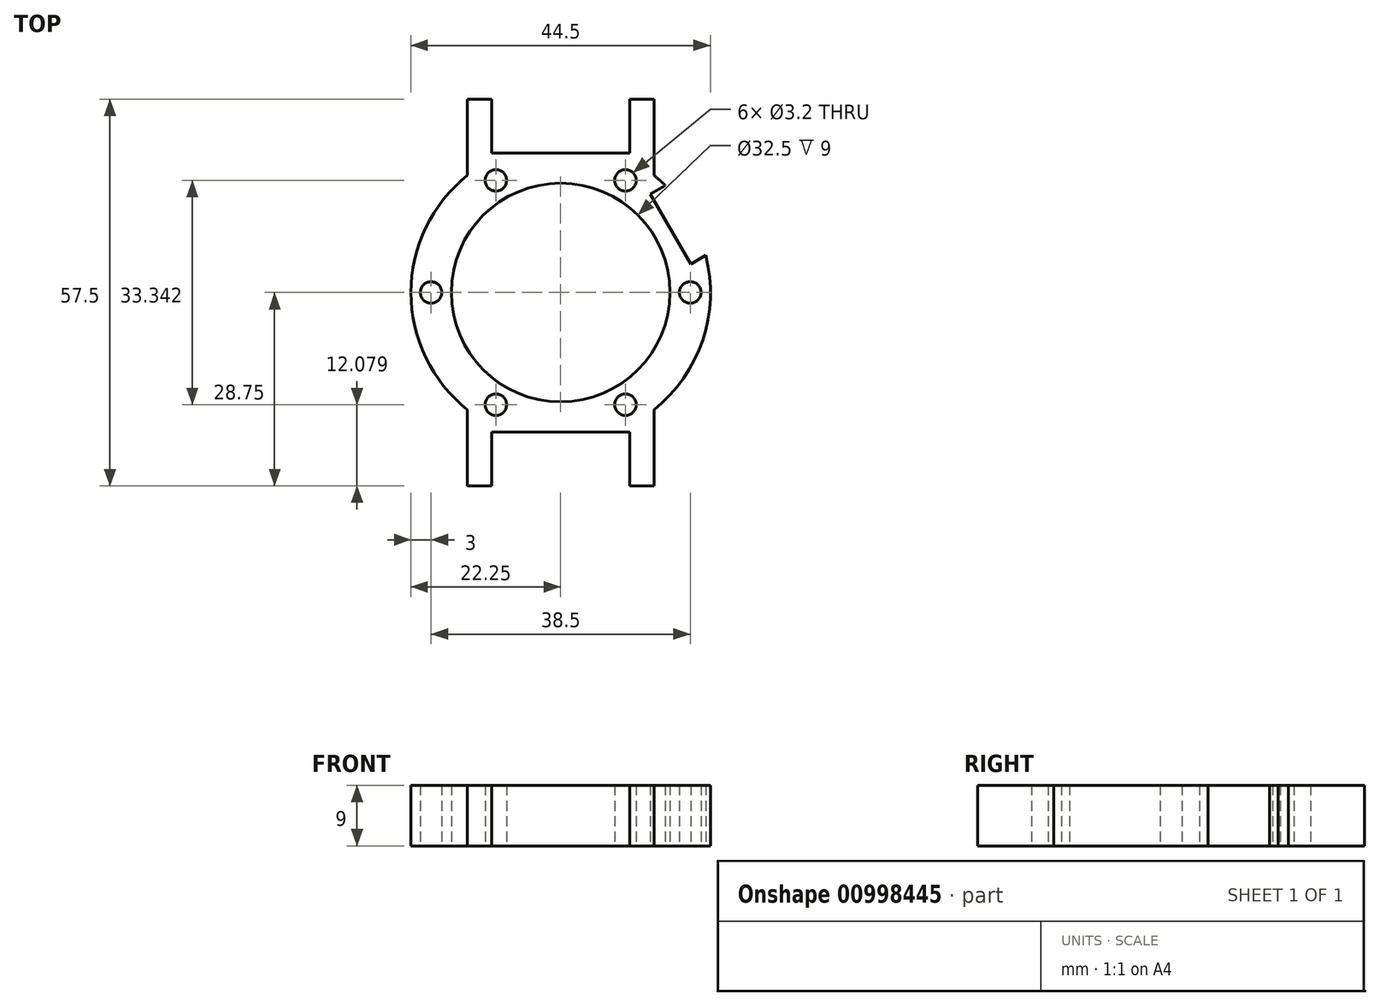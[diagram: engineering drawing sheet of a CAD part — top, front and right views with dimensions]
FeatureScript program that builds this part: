
annotation { "Feature Type Name" : "Feature", "Feature Type Description" : "" }
export const myFeature = defineFeature(function(context is Context, id is Id, definition is map)
    precondition{}
    {
        {
            var Q0;
            Q0=qCreatedBy(makeId("Top.planeOp"),FACE);
            var sketch = newSketch(context, id + "F0", { "sketchPlane" : qUnion([Q0])});
            skCircle(sketch, "E0.cCircle", {"center": v(0, 0) * mm, "radius": 16.67 * mm, "construction": true});
            skLineSegment(sketch, "E0.0", {"start": v(9.62, -16.67) * mm, "end": v(-9.62, -16.67) * mm, "construction": true});
            skLineSegment(sketch, "E0.1", {"start": v(-9.62, -16.67) * mm, "end": v(-19.25, 0) * mm, "construction": true});
            skLineSegment(sketch, "E0.2", {"start": v(-19.25, 0) * mm, "end": v(-9.62, 16.67) * mm, "construction": true});
            skLineSegment(sketch, "E0.3", {"start": v(-9.63, 16.67) * mm, "end": v(9.62, 16.67) * mm, "construction": true});
            skLineSegment(sketch, "E0.4", {"start": v(9.62, 16.67) * mm, "end": v(19.25, 0) * mm, "construction": true});
            skLineSegment(sketch, "E0.5", {"start": v(19.25, 0) * mm, "end": v(9.62, -16.67) * mm, "construction": true});
            skPoint(sketch, "E0.0.midPoint", {"position": v(0, -16.67) * mm});
            skCircle(sketch, "E1", {"center": v(0, 0) * mm, "radius": 16.25 * mm});
            skCircle(sketch, "E2", {"center": v(0, 0) * mm, "radius": 22.25 * mm});
            skLineSegment(sketch, "E3.bottom", {"start": v(10.25, 20.75) * mm, "end": v(-10.25, 20.75) * mm});
            skLineSegment(sketch, "E3.top", {"start": v(10.25, 28.75) * mm, "end": v(-10.25, 28.75) * mm});
            skLineSegment(sketch, "E3.left", {"start": v(10.25, 20.75) * mm, "end": v(10.25, 28.75) * mm});
            skLineSegment(sketch, "E3.right", {"start": v(-10.25, 20.75) * mm, "end": v(-10.25, 28.75) * mm});
            skPoint(sketch, "E3.middle", {"position": v(0, 24.75) * mm});
            skLineSegment(sketch, "E4.bottom", {"start": v(13.85, 28.75) * mm, "end": v(-13.85, 28.75) * mm});
            skLineSegment(sketch, "E4.top", {"start": v(13.85, 17.41) * mm, "end": v(-13.85, 17.41) * mm});
            skLineSegment(sketch, "E4.left", {"start": v(13.85, 28.75) * mm, "end": v(13.85, 17.41) * mm});
            skLineSegment(sketch, "E4.right", {"start": v(-13.85, 28.75) * mm, "end": v(-13.85, 17.41) * mm});
            skPoint(sketch, "E4.middle", {"position": v(0, 23.08) * mm});
            skLineSegment(sketch, "E5.bottom", {"start": v(10.25, -28.75) * mm, "end": v(-10.25, -28.75) * mm});
            skLineSegment(sketch, "E5.top", {"start": v(10.25, -20.75) * mm, "end": v(-10.25, -20.75) * mm});
            skLineSegment(sketch, "E5.left", {"start": v(10.25, -28.75) * mm, "end": v(10.25, -20.75) * mm});
            skLineSegment(sketch, "E5.right", {"start": v(-10.25, -28.75) * mm, "end": v(-10.25, -20.75) * mm});
            skPoint(sketch, "E5.middle", {"position": v(0, -24.75) * mm});
            skLineSegment(sketch, "E6.bottom", {"start": v(13.85, -28.75) * mm, "end": v(-13.85, -28.75) * mm});
            skLineSegment(sketch, "E6.top", {"start": v(13.85, -17.41) * mm, "end": v(-13.85, -17.41) * mm});
            skLineSegment(sketch, "E6.left", {"start": v(13.85, -28.75) * mm, "end": v(13.85, -17.41) * mm});
            skLineSegment(sketch, "E6.right", {"start": v(-13.85, -28.75) * mm, "end": v(-13.85, -17.41) * mm});
            skPoint(sketch, "E6.middle", {"position": v(0, -23.08) * mm});
            skLineSegment(sketch, "E7", {"start": v(13.32, 14.62) * mm, "end": v(19.32, 4.23) * mm});
            skLineSegment(sketch, "E8", {"start": v(13.32, 14.62) * mm, "end": v(15.56, 15.9) * mm});
            skLineSegment(sketch, "E9", {"start": v(19.32, 4.23) * mm, "end": v(21.56, 5.52) * mm});
            skLineSegment(sketch, "E10", {"start": v(13.32, 14.62) * mm, "end": v(0, 0) * mm, "construction": true});
            skLineSegment(sketch, "E11", {"start": v(0, 0) * mm, "end": v(19.32, 4.23) * mm, "construction": true});
            skSolve(sketch);
        }
        {
            var Q0;
            Q0=makeQuery(id+"F0.imprint","IMPRINT",FACE,{"disambiguationData":[TD([[makeQuery(id+"F0.imprint","IMPRINT",EDGE,{"derivedFrom":sQuery(id+"F0.wireOp",EDGE,"E1")}),-1.0]])]});
            var Q1;
            {var subQ1=sQuery(id+"F0.wireOp",EDGE,"E5.right");Q1=makeQuery(id+"F0.imprint","IMPRINT",FACE,{"disambiguationData":[TD([[makeQuery(id+"F0.imprint","IMPRINT",EDGE,{"derivedFrom":subQ1}),1.0]])]});}
            var Q2;
            {var subQ0=sQuery(id+"F0.wireOp",EDGE,"E6.top");Q2=makeQuery(id+"F0.imprint","IMPRINT",FACE,{"disambiguationData":[TD([[makeQuery(id+"F0.imprint","IMPRINT",EDGE,{"derivedFrom":subQ0}),1.0]])]});}
            var Q3;
            {var subQ1=sQuery(id+"F0.wireOp",EDGE,"E5.left");Q3=makeQuery(id+"F0.imprint","IMPRINT",FACE,{"disambiguationData":[TD([[makeQuery(id+"F0.imprint","IMPRINT",EDGE,{"derivedFrom":subQ1}),-1.0]])]});}
            var Q4;
            {var subQ0=sQuery(id+"F0.wireOp",EDGE,"E3.left");Q4=makeQuery(id+"F0.imprint","IMPRINT",FACE,{"disambiguationData":[TD([[makeQuery(id+"F0.imprint","IMPRINT",EDGE,{"derivedFrom":subQ0}),-1.0]])]});}
            var Q5;
            {var subQ3=sQuery(id+"F0.wireOp",EDGE,"E4.top");Q5=makeQuery(id+"F0.imprint","IMPRINT",FACE,{"disambiguationData":[TD([[makeQuery(id+"F0.imprint","IMPRINT",EDGE,{"derivedFrom":subQ3}),-1.0]])]});}
            var Q6;
            {var subQ0=sQuery(id+"F0.wireOp",EDGE,"E3.right");Q6=makeQuery(id+"F0.imprint","IMPRINT",FACE,{"disambiguationData":[TD([[makeQuery(id+"F0.imprint","IMPRINT",EDGE,{"derivedFrom":subQ0}),1.0]])]});}
            extrude(context, id + "F1", {"entities" : qUnion([Q0, Q1, Q2, Q3, Q4, Q5, Q6]), "depth" : 9 * mm, "offsetDistance" : 25 * mm});
        }
        {
            var Q0;
            Q0=sQuery(id+"F0.wireOp",VERTEX,"E0.0.end");
            var Q1;
            Q1=sQuery(id+"F0.wireOp",VERTEX,"E0.0.start");
            var Q2;
            Q2=sQuery(id+"F0.wireOp",VERTEX,"E0.4.end");
            var Q3;
            Q3=sQuery(id+"F0.wireOp",VERTEX,"E0.3.end");
            var Q4;
            Q4=sQuery(id+"F0.wireOp",VERTEX,"E0.2.end");
            var Q5;
            Q5=sQuery(id+"F0.wireOp",VERTEX,"E0.1.end");
            var Q6;
            Q6=makeQuery(id+"F1.opExtrude","SWEPT_BODY",BODY,{"disambiguationData":[OSD([sQuery(id+"F0.wireOp",EDGE,"E1"),sQuery(id+"F0.wireOp",EDGE,"E2"),sQuery(id+"F0.wireOp",EDGE,"E3.bottom"),sQuery(id+"F0.wireOp",EDGE,"E3.left"),sQuery(id+"F0.wireOp",EDGE,"E3.right"),sQuery(id+"F0.wireOp",EDGE,"E4.bottom"),sQuery(id+"F0.wireOp",EDGE,"E4.left"),sQuery(id+"F0.wireOp",EDGE,"E4.right"),sQuery(id+"F0.wireOp",EDGE,"E5.top"),sQuery(id+"F0.wireOp",EDGE,"E5.left"),sQuery(id+"F0.wireOp",EDGE,"E5.right"),sQuery(id+"F0.wireOp",EDGE,"E6.bottom"),sQuery(id+"F0.wireOp",EDGE,"E6.left"),sQuery(id+"F0.wireOp",EDGE,"E6.right"),sQuery(id+"F0.wireOp",EDGE,"E7"),sQuery(id+"F0.wireOp",EDGE,"E8"),sQuery(id+"F0.wireOp",EDGE,"E9")])]});
            hole(context, id + "F2", {"style" : HoleStyle.SIMPLE, "endStyle" : HoleEndStyle.BLIND, "oppositeDirection" : true, "holeDiameter" : 3.2 * mm, "majorDiameter" : 5 * mm, "holeDepth" : 40 * mm, "isTappedThrough" : true, "tappedDepth" : 12 * mm, "tapClearance" : 3, "locations" : qUnion([Q0, Q1, Q2, Q3, Q4, Q5]), "scope" : qUnion([Q6])});
        }
    });
